# Revit family: РОСМА_МанометрТочныхИзмерений
name_source: partatom
category: Арматура трубопроводов
revit_build: Autodesk Revit 2018 (Build: 20180423_1000(x64)
units: mm (PartAtom-declared; Revit-internal decimal feet)

## family parameters
Всегда вертикально = Да
На основе рабочей плоскости = Нет
Общий = Нет
При загрузке вырезать с полостями = Нет
Размер круглого соединителя = Использовать диаметр
Тип детали = Вставляется

## types (1)
- 610
    ADSK_Единица измерения = шт.
    ADSK_Количество = 1
    D = 150 мм
    D1 = 151 мм
    D2 = 149 мм
    D2/2 = 75 мм
    Dполости_переднСт = 144 мм
    G = 20 мм
    R1_шкала = 65 мм
    R2_шкала = 64 мм
    R_лого = 50 мм
    S = 27 мм
    Table = спец_МТИ
    URL = https://rosma.spb.ru
    b = 51 мм
    b-e = 5 мм
    e = 15 мм
    f = 21 мм
    h = 115 мм
    Гарантийный срок = 18 месяцев
    Группа модели = Оборудование
    Давление01 = ‎ : ТМ 0…0,06МПа
    Давление02 = ‎ : ТМ 0…0,1МПа
    Давление03 = ‎ : ТМ 0…0,16МПа
    Давление04 = ‎ : ТМ 0…0,25МПа
    Давление05 = ‎ : ТМ 0…0,4МПа
    Давление06 = ‎ : ТМ 0…0,6МПа
    Давление07 = ‎ : ТМ 0…1,0МПа
    Давление08 = ‎ : ТМ 0…1,6МПа
    Давление09 = ‎ : ТМ 0…2,5МПа
    Давление10 = ‎ : ТМ 0…4МПа
    Давление11 = ‎ : ТМ 0…6МПа
    Давление12 = ‎ : ТМ 0…10МПа
    Давление13 = ‎ : ТМ 0…16МПа
    Давление14 = ‎ : ТМ 0…25МПа
    Давление15 = ‎ : ТМ 0…40МПа
    Давление16 = ‎ : ТМ 0…60МПа
    Давление17 = ‎ : ТМ 0…100МПа
    Давление18 = ‎ : ТМВ -0,1…0,06МПа
    Давление19 = ‎ : ТМВ -0,1…0,15МПа
    Давление20 = ‎ : ТМВ -0,1…0,3МПа
    Давление21 = ‎ : ТМВ -0,1…0,5МПа
    Давление22 = ‎ : ТМВ -0,1…0,9МПа
    Давление23 = ‎ : ТМВ -0,1…1,5МПа
    Давление24 = ‎ : ТМВ -0,1…2,4МПа
    Диапазон рабочих температур при поверке = от +18°С до +28°С
    Длина стрелки = 65 мм
    Изготовитель = ЗАО "РОСМА"
    КлассТочности01 = ‎    : 0,4
    КлассТочности02 = ‎    : 0,6
    КлассТочности03 = ‎    : 1
    Климатическое исполнение = Группа В3 по ГОСТ Р 52931; климатическое исполнение УХЛ категории 3.1 по ГОСТ 15150
    Код IP = IP40
    Описание = Манометр показывающий ТМ, МТИ, точных измерений, может быть использован в качестве рабочего эталона при поверке и калибровке средств измерения давления с соблюдением требований по соответствию классов точности образцового и поверяемого приборов.
    Присоединение = Радиальное
    Температура окружающей среды = от -60°С до +60°С
    Температура рабочей среды = от -30°С до +100°С
    Техническая документация = ТУ 4212-001-4719015564-2008; ГОСТ 2405–88
